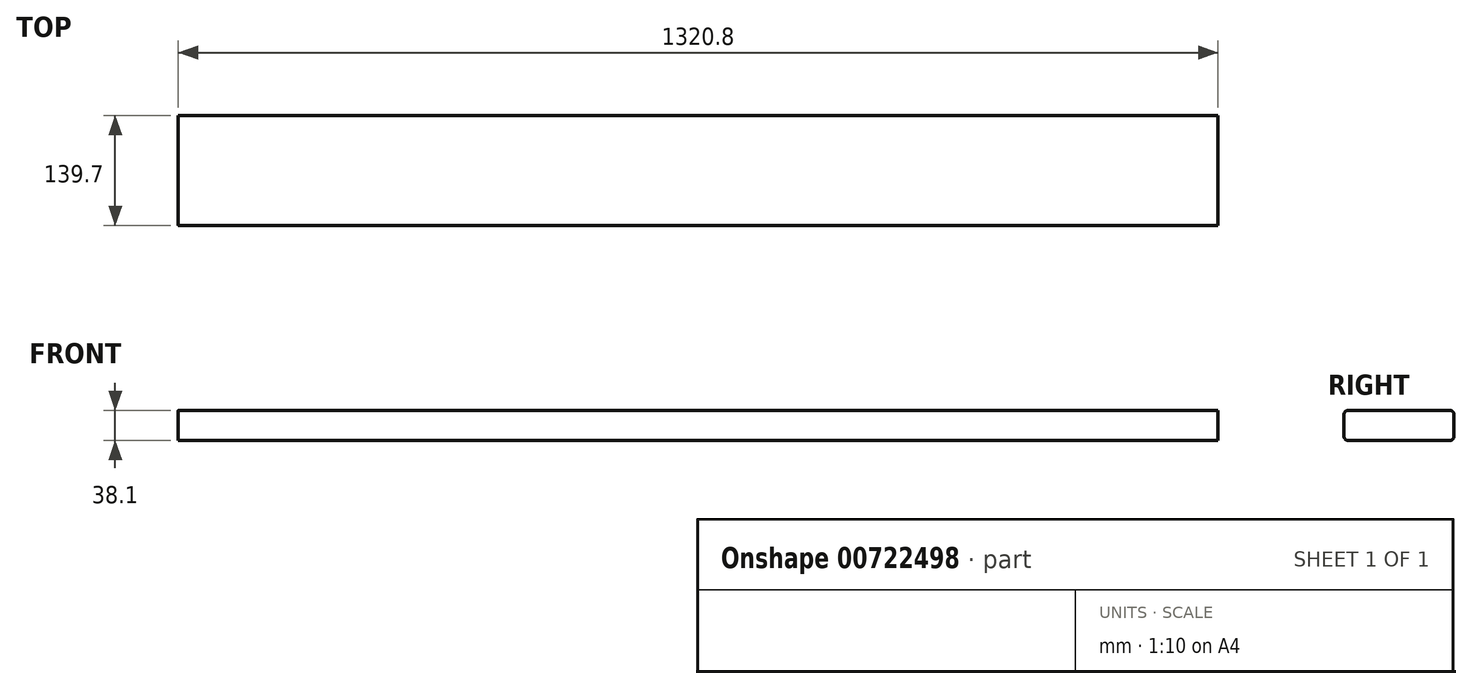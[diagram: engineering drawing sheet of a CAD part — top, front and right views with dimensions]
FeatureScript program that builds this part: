
annotation { "Feature Type Name" : "Feature", "Feature Type Description" : "" }
export const myFeature = defineFeature(function(context is Context, id is Id, definition is map)
    precondition{}
    {
        {
            var Q0;
            Q0=qCreatedBy(makeId("Top.planeOp"),FACE);
            var sketch = newSketch(context, id + "F0", { "sketchPlane" : qUnion([Q0])});
            skLineSegment(sketch, "E0", {"start": v(0, 0) * mm, "end": v(0, -139.7) * mm});
            skLineSegment(sketch, "E1", {"start": v(0, -139.7) * mm, "end": v(1320.8, -139.7) * mm});
            skLineSegment(sketch, "E2", {"start": v(1320.8, -139.7) * mm, "end": v(1320.8, 0) * mm});
            skLineSegment(sketch, "E3", {"start": v(1320.8, 0) * mm, "end": v(0, 0) * mm});
            skSolve(sketch);
        }
        {
            var Q0;
            Q0 = qSketchRegion(id + "F0", true);
            extrude(context, id + "F1", {"entities" : qUnion([Q0]), "depth" : 38.1 * mm, "offsetDistance" : 25.4 * mm});
        }
        {
            var Q0;
            Q0=makeQuery(id+"F1.opExtrude","CAP_EDGE",EDGE,{"disambiguationData":[OSD([sQuery(id+"F0.wireOp",EDGE,"E1")])],"isStart":false});
            var Q1;
            Q1=makeQuery(id+"F1.opExtrude","CAP_EDGE",EDGE,{"disambiguationData":[OSD([sQuery(id+"F0.wireOp",EDGE,"E1")])],"isStart":true});
            var Q2;
            Q2=makeQuery(id+"F1.opExtrude","CAP_EDGE",EDGE,{"disambiguationData":[OSD([sQuery(id+"F0.wireOp",EDGE,"E3")])],"isStart":false});
            var Q3;
            Q3=makeQuery(id+"F1.opExtrude","CAP_EDGE",EDGE,{"disambiguationData":[OSD([sQuery(id+"F0.wireOp",EDGE,"E3")])],"isStart":true});
            fillet(context, id + "F2", {"entities" : qUnion([Q0, Q1, Q2, Q3]), "radius" : 5.08 * mm, "tangentPropagation" : true, "allowEdgeOverflow" : false});
        }
    });
